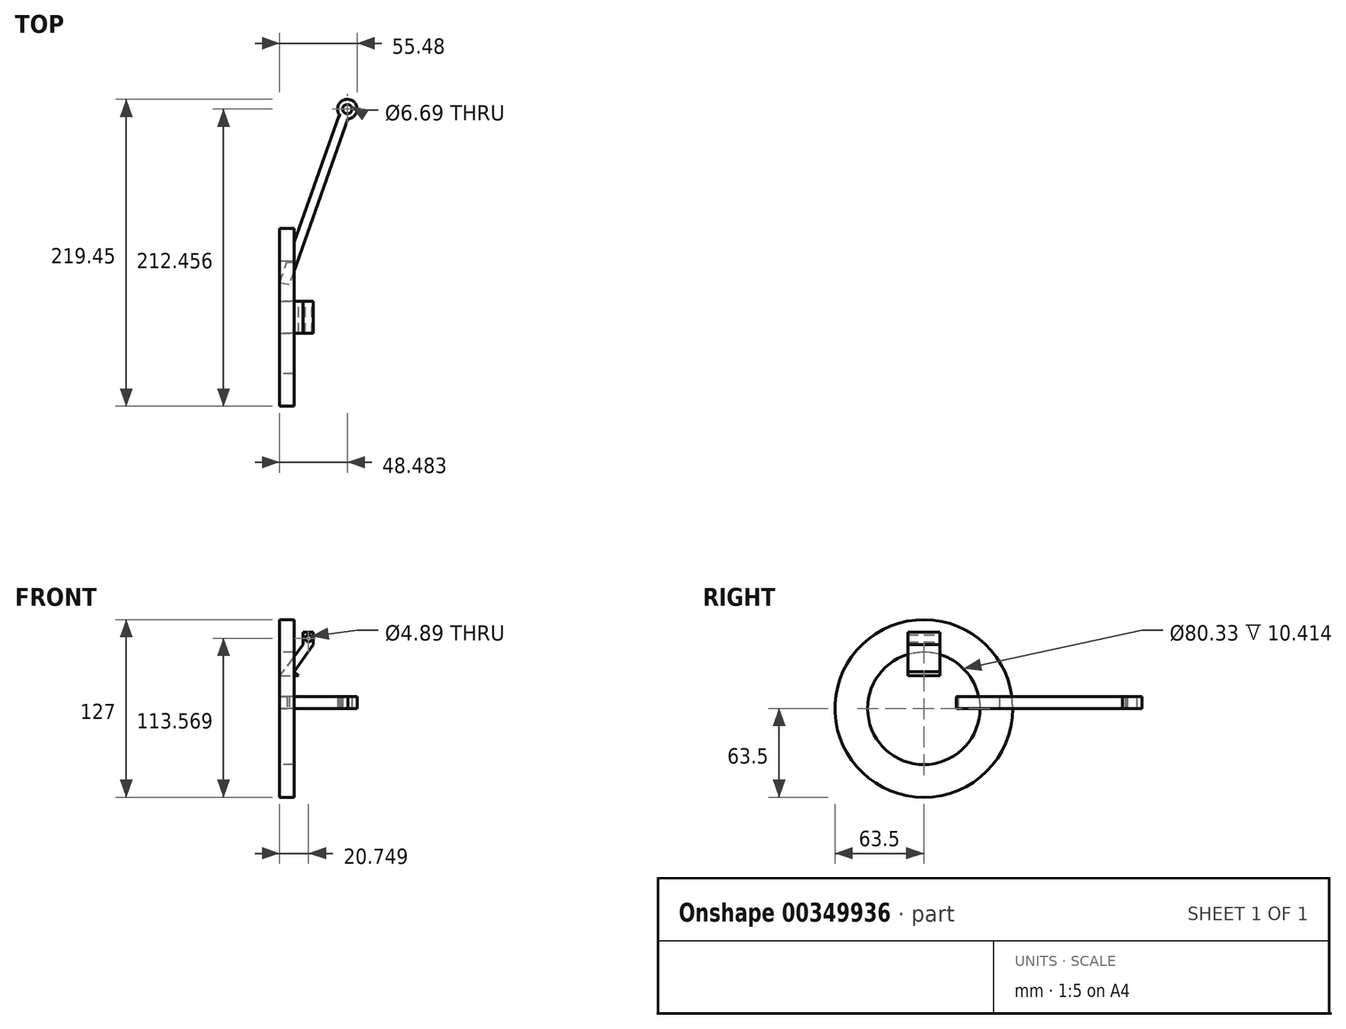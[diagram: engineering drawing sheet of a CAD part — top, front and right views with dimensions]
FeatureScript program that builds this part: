
annotation { "Feature Type Name" : "Feature", "Feature Type Description" : "" }
export const myFeature = defineFeature(function(context is Context, id is Id, definition is map)
    precondition{}
    {
        {
            var Q0;
            Q0=qCreatedBy(makeId("Right.planeOp"),FACE);
            var sketch = newSketch(context, id + "F0", { "sketchPlane" : qUnion([Q0])});
            skCircle(sketch, "E0", {"center": v(0, 0) * mm, "radius": 63.5 * mm});
            skCircle(sketch, "E1", {"center": v(0, 0) * mm, "radius": 40.17 * mm});
            skSolve(sketch);
        }
        {
            var Q0;
            Q0=qCreatedBy(makeId("Top.planeOp"),FACE);
            var sketch = newSketch(context, id + "F1", { "sketchPlane" : qUnion([Q0])});
            skLineSegment(sketch, "E2", {"start": v(0, 24.62) * mm, "end": v(42.5, 144.3) * mm});
            skLineSegment(sketch, "E3", {"start": v(42.5, 144.3) * mm, "end": v(49.01, 141.98) * mm});
            skLineSegment(sketch, "E4", {"start": v(49.01, 141.98) * mm, "end": v(6.92, 23.44) * mm});
            skLineSegment(sketch, "E5", {"start": v(6.92, 23.44) * mm, "end": v(0, 24.62) * mm});
            skCircle(sketch, "E6", {"center": v(48.48, 148.96) * mm, "radius": 7 * mm});
            skCircle(sketch, "E7", {"center": v(48.48, 148.96) * mm, "radius": 3.34 * mm});
            skSolve(sketch);
        }
        {
            var Q0;
            Q0 = qSketchRegion(id + "F1", true);
            extrude(context, id + "F2", {"entities" : qUnion([Q0]), "depth" : 8.64 * mm, "offsetDistance" : 25.4 * mm});
        }
        {
            var Q0;
            Q0 = qSketchRegion(id + "F0", true);
            extrude(context, id + "F3", {"entities" : qUnion([Q0]), "operationType" : NewBodyOperationType.ADD, "depth" : 10.4 * mm, "offsetDistance" : 25.4 * mm});
        }
        {
            var Q0;
            Q0=qCreatedBy(makeId("Front.planeOp"),FACE);
            var sketch = newSketch(context, id + "F4", { "sketchPlane" : qUnion([Q0])});
            skLineSegment(sketch, "E8", {"start": v(10.48, 26.28) * mm, "end": v(24.12, 45.58) * mm});
            skLineSegment(sketch, "E9", {"start": v(24.12, 45.58) * mm, "end": v(24.12, 54.56) * mm});
            skLineSegment(sketch, "E10", {"start": v(24.12, 54.56) * mm, "end": v(16.8, 54.56) * mm});
            skLineSegment(sketch, "E11", {"start": v(16.8, 54.56) * mm, "end": v(16.8, 45.58) * mm});
            skLineSegment(sketch, "E12", {"start": v(16.8, 45.58) * mm, "end": v(0, 23.29) * mm});
            skLineSegment(sketch, "E13", {"start": v(0, 23.29) * mm, "end": v(13.47, 23.29) * mm});
            skLineSegment(sketch, "E14", {"start": v(13.47, 23.29) * mm, "end": v(10.48, 26.28) * mm});
            skSolve(sketch);
        }
        {
            var Q0;
            Q0 = qSketchRegion(id + "F4", true);
            extrude(context, id + "F5", {"entities" : qUnion([Q0]), "operationType" : NewBodyOperationType.ADD, "endBound" : BoundingType.SYMMETRIC, "depth" : 22.86 * mm, "offsetDistance" : 25.4 * mm});
        }
        {
            var Q0;
            Q0=makeQuery(id+"F5.opExtrude","CAP_FACE",FACE,{"disambiguationData":[OSD([sQuery(id+"F4.wireOp",EDGE,"E8"),sQuery(id+"F4.wireOp",EDGE,"E9"),sQuery(id+"F4.wireOp",EDGE,"E10"),sQuery(id+"F4.wireOp",EDGE,"E11"),sQuery(id+"F4.wireOp",EDGE,"E12"),sQuery(id+"F4.wireOp",EDGE,"E13"),sQuery(id+"F4.wireOp",EDGE,"E14")])],"isStart":true});
            var sketch = newSketch(context, id + "F6", { "sketchPlane" : qUnion([Q0])});
            skCircle(sketch, "E15", {"center": v(-20.75, 50.07) * mm, "radius": 2.44 * mm});
            skPoint(sketch, "E15.centerSnap0", {"position": v(-24.12, 50.07) * mm});
            skSolve(sketch);
        }
        {
            var Q0;
            Q0 = qSketchRegion(id + "F6", true);
            extrude(context, id + "F7", {"entities" : qUnion([Q0]), "operationType" : NewBodyOperationType.REMOVE, "oppositeDirection" : true, "depth" : 27.94 * mm, "offsetDistance" : 25.4 * mm});
        }
    });
